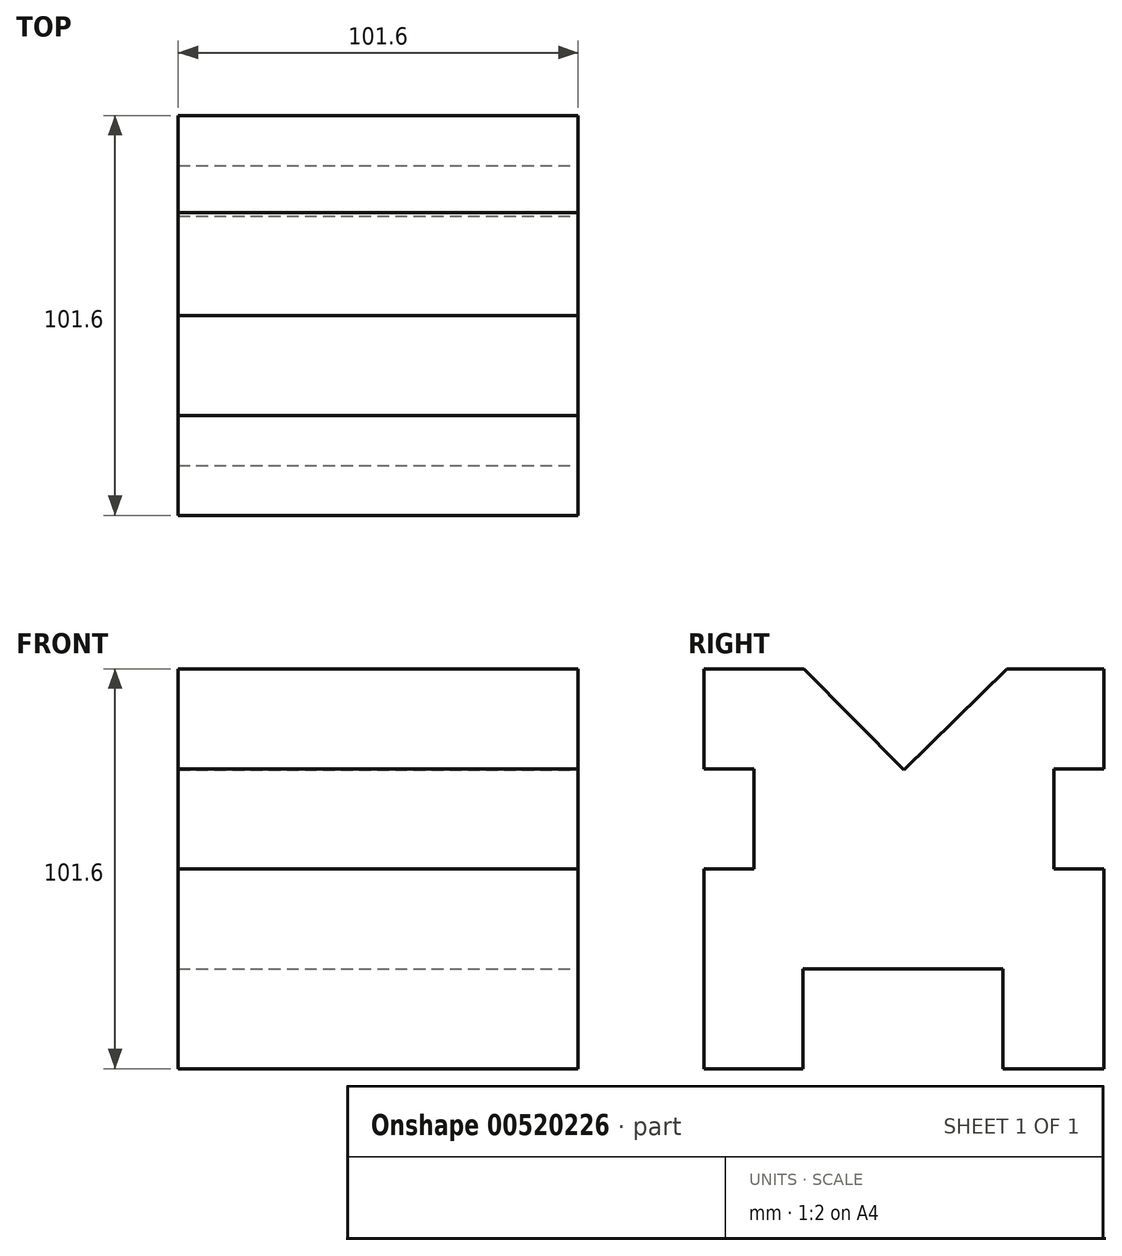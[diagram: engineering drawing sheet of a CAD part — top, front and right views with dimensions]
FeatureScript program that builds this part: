
annotation { "Feature Type Name" : "Feature", "Feature Type Description" : "" }
export const myFeature = defineFeature(function(context is Context, id is Id, definition is map)
    precondition{}
    {
        {
            var Q0;
            Q0=qCreatedBy(makeId("Top.planeOp"),FACE);
            var sketch = newSketch(context, id + "F0", { "sketchPlane" : qUnion([Q0])});
            skLineSegment(sketch, "E0.bottom", {"start": v(0, 0) * mm, "end": v(-101.6, 0) * mm});
            skLineSegment(sketch, "E0.top", {"start": v(0, -101.6) * mm, "end": v(-101.6, -101.6) * mm});
            skLineSegment(sketch, "E0.left", {"start": v(0, 0) * mm, "end": v(0, -101.6) * mm});
            skLineSegment(sketch, "E0.right", {"start": v(-101.6, 0) * mm, "end": v(-101.6, -101.6) * mm});
            skSolve(sketch);
        }
        {
            var Q0;
            Q0 = qSketchRegion(id + "F0", true);
            extrude(context, id + "F1", {"entities" : qUnion([Q0]), "depth" : 101.6 * mm, "offsetDistance" : 25.4 * mm});
        }
        {
            var Q0;
            Q0=makeQuery(id+"F1.opExtrude","SWEPT_FACE",FACE,{"disambiguationData":[OSD([sQuery(id+"F0.wireOp",EDGE,"E0.left")])]});
            var sketch = newSketch(context, id + "F2", { "sketchPlane" : qUnion([Q0])});
            skLineSegment(sketch, "E1", {"start": v(-101.6, 50.8) * mm, "end": v(-88.9, 50.8) * mm});
            skLineSegment(sketch, "E2", {"start": v(-88.9, 50.8) * mm, "end": v(-88.9, 76.2) * mm});
            skLineSegment(sketch, "E3", {"start": v(-88.9, 76.2) * mm, "end": v(-101.6, 76.2) * mm});
            skLineSegment(sketch, "E4", {"start": v(-101.6, 101.6) * mm, "end": v(-76.2, 101.6) * mm});
            skLineSegment(sketch, "E5", {"start": v(-50.8, 101.6) * mm, "end": v(-50.8, 0) * mm});
            skLineSegment(sketch, "E6", {"start": v(-76.2, 101.6) * mm, "end": v(-50.8, 75.86) * mm});
            skLineSegment(sketch, "E7", {"start": v(-50.8, 75.86) * mm, "end": v(-24.7, 101.6) * mm});
            skLineSegment(sketch, "E8", {"start": v(0, 50.8) * mm, "end": v(-12.7, 50.8) * mm});
            skLineSegment(sketch, "E9", {"start": v(-12.7, 50.8) * mm, "end": v(-12.7, 76.2) * mm});
            skLineSegment(sketch, "E10", {"start": v(-12.7, 76.2) * mm, "end": v(0, 76.2) * mm});
            skLineSegment(sketch, "E11", {"start": v(-76.44, 0) * mm, "end": v(-76.44, 25.4) * mm});
            skLineSegment(sketch, "E12", {"start": v(-76.44, 25.4) * mm, "end": v(-25.64, 25.4) * mm});
            skLineSegment(sketch, "E13", {"start": v(-25.64, 25.4) * mm, "end": v(-25.64, 0) * mm});
            skSolve(sketch);
        }
        {
            var Q0;
            Q0 = qSketchRegion(id + "F2", true);
            var Q1;
            {var subQ3=sQuery(id+"F2.wireOp",EDGE,"E6");Q1=makeQuery(id+"F2.imprint","IMPRINT",FACE,{"disambiguationData":[TD([[makeQuery(id+"F2.imprint","IMPRINT",EDGE,{"derivedFrom":subQ3}),1.0]])]});}
            var Q2;
            {var subQ3=sQuery(id+"F2.wireOp",EDGE,"E7");Q2=makeQuery(id+"F2.imprint","IMPRINT",FACE,{"disambiguationData":[TD([[makeQuery(id+"F2.imprint","IMPRINT",EDGE,{"derivedFrom":subQ3}),1.0]])]});}
            var Q3;
            {var subQ0=sQuery(id+"F2.wireOp",EDGE,"E1");Q3=makeQuery(id+"F2.imprint","IMPRINT",FACE,{"disambiguationData":[TD([[makeQuery(id+"F2.imprint","IMPRINT",EDGE,{"derivedFrom":subQ0}),1.0]])]});}
            var Q4;
            {var subQ5=sQuery(id+"F2.wireOp",EDGE,"E11");Q4=makeQuery(id+"F2.imprint","IMPRINT",FACE,{"disambiguationData":[TD([[makeQuery(id+"F2.imprint","IMPRINT",EDGE,{"derivedFrom":subQ5}),-1.0]])]});}
            var Q5;
            {var subQ5=sQuery(id+"F2.wireOp",EDGE,"E13");Q5=makeQuery(id+"F2.imprint","IMPRINT",FACE,{"disambiguationData":[TD([[makeQuery(id+"F2.imprint","IMPRINT",EDGE,{"derivedFrom":subQ5}),-1.0]])]});}
            var Q6;
            {var subQ0=sQuery(id+"F2.wireOp",EDGE,"E8");Q6=makeQuery(id+"F2.imprint","IMPRINT",FACE,{"disambiguationData":[TD([[makeQuery(id+"F2.imprint","IMPRINT",EDGE,{"derivedFrom":subQ0}),-1.0]])]});}
            extrude(context, id + "F3", {"entities" : qUnion([Q0, Q1, Q2, Q3, Q4, Q5, Q6]), "operationType" : NewBodyOperationType.REMOVE, "oppositeDirection" : true, "depth" : 101.6 * mm, "offsetDistance" : 25.4 * mm});
        }
    });
